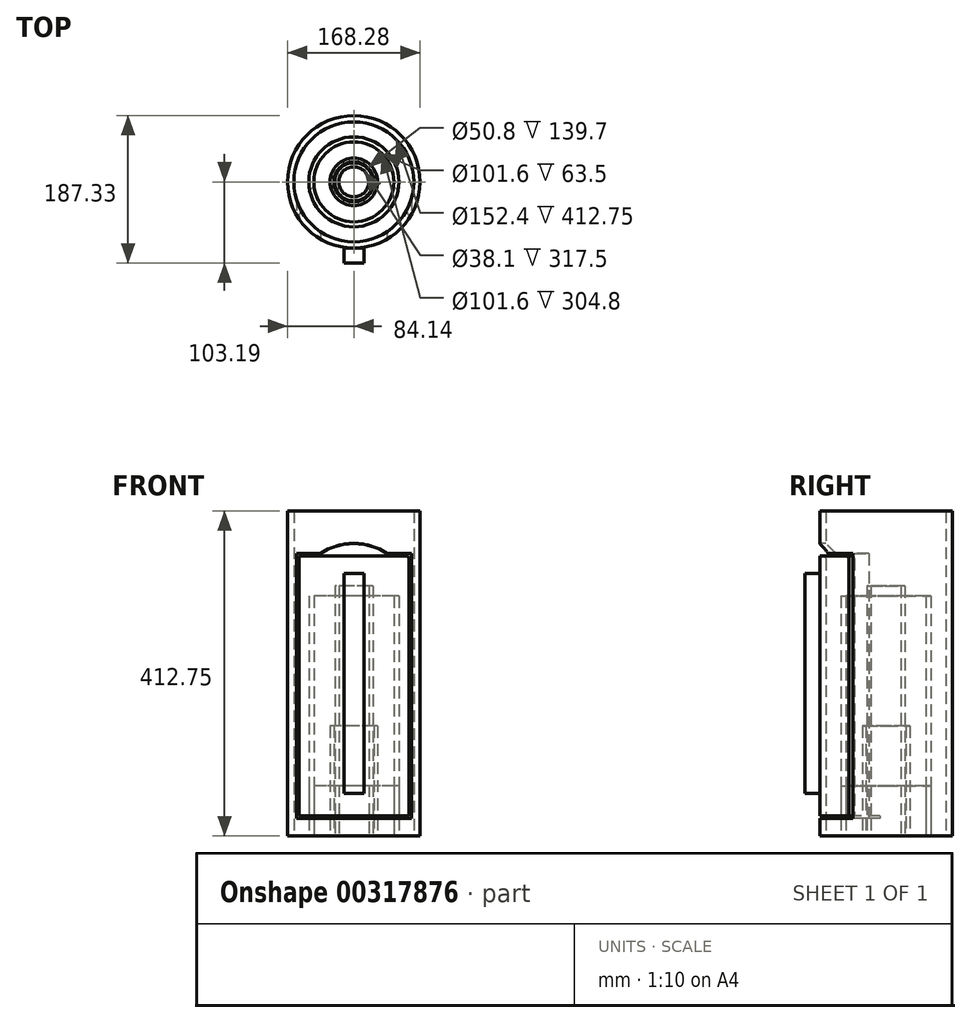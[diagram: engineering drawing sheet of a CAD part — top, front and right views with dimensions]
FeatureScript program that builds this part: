
annotation { "Feature Type Name" : "Feature", "Feature Type Description" : "" }
export const myFeature = defineFeature(function(context is Context, id is Id, definition is map)
    precondition{}
    {
        {
            var Q0;
            Q0=qCreatedBy(makeId("Top.planeOp"),FACE);
            var sketch = newSketch(context, id + "F0", { "sketchPlane" : qUnion([Q0])});
            skCircle(sketch, "E0", {"center": v(0, 0) * mm, "radius": 76.2 * mm});
            skCircle(sketch, "E1", {"center": v(0, 0) * mm, "radius": 84.14 * mm});
            skSolve(sketch);
        }
        {
            var Q0;
            Q0=makeQuery(id+"F0.imprint","IMPRINT",FACE,{"disambiguationData":[TD([[makeQuery(id+"F0.imprint","IMPRINT",EDGE,{"derivedFrom":sQuery(id+"F0.wireOp",EDGE,"E0")}),-1.0]])]});
            extrude(context, id + "F1", {"entities" : qUnion([Q0]), "depth" : 412.75 * mm});
        }
        {
            var Q0;
            Q0=qCreatedBy(makeId("Top.planeOp"),FACE);
            var sketch = newSketch(context, id + "F2", { "sketchPlane" : qUnion([Q0])});
            skCircle(sketch, "E2", {"center": v(0, 0) * mm, "radius": 50.8 * mm});
            skCircle(sketch, "E3", {"center": v(0, 0) * mm, "radius": 57.15 * mm});
            skSolve(sketch);
        }
        {
            var Q0;
            Q0=makeQuery(id+"F2.imprint","IMPRINT",FACE,{"disambiguationData":[TD([[makeQuery(id+"F2.imprint","IMPRINT",EDGE,{"derivedFrom":sQuery(id+"F2.wireOp",EDGE,"E2")}),-1.0]])]});
            extrude(context, id + "F3", {"entities" : qUnion([Q0]), "depth" : 63.5 * mm});
        }
        {
            var Q0;
            Q0=qCreatedBy(makeId("Top.planeOp"),FACE);
            var sketch = newSketch(context, id + "F4", { "sketchPlane" : qUnion([Q0])});
            skCircle(sketch, "E4", {"center": v(0, 0) * mm, "radius": 25.4 * mm});
            skCircle(sketch, "E5", {"center": v(0, 0) * mm, "radius": 30.16 * mm});
            skSolve(sketch);
        }
        {
            var Q0;
            Q0=makeQuery(id+"F4.imprint","IMPRINT",FACE,{"disambiguationData":[TD([[makeQuery(id+"F4.imprint","IMPRINT",EDGE,{"derivedFrom":sQuery(id+"F4.wireOp",EDGE,"E4")}),-1.0]])]});
            extrude(context, id + "F5", {"entities" : qUnion([Q0]), "depth" : 139.7 * mm});
        }
        {
            var Q0;
            Q0=qSketchRegion(id+"F2",true);
            extrude(context, id + "F6", {"entities" : qUnion([Q0]), "depth" : 304.8 * mm});
        }
        {
            var Q0;
            Q0=qCreatedBy(makeId("Top.planeOp"),FACE);
            var sketch = newSketch(context, id + "F7", { "sketchPlane" : qUnion([Q0])});
            skCircle(sketch, "E6", {"center": v(0, 0) * mm, "radius": 19.05 * mm});
            skCircle(sketch, "E7", {"center": v(0, 0) * mm, "radius": 24.13 * mm});
            skSolve(sketch);
        }
        {
            var Q0;
            Q0=makeQuery(id+"F7.imprint","IMPRINT",FACE,{"disambiguationData":[TD([[makeQuery(id+"F7.imprint","IMPRINT",EDGE,{"derivedFrom":sQuery(id+"F7.wireOp",EDGE,"E6")}),-1.0]])]});
            extrude(context, id + "F8", {"entities" : qUnion([Q0]), "depth" : 317.5 * mm});
        }
        {
            var Q0;
            Q0=qCreatedBy(makeId("Front.planeOp"),FACE);
            cPlane(context, id + "F9", {"entities" : qUnion([Q0]), "cplaneType" : CPlaneType.OFFSET, "offset" : 84.14 * mm, "width" : 152.4 * mm, "height" : 152.4 * mm});
        }
        {
            var Q0;
            Q0=qCreatedBy(id+"F9.planeOp",FACE);
            var sketch = newSketch(context, id + "F10", { "sketchPlane" : qUnion([Q0])});
            skLineSegment(sketch, "E8.bottom", {"start": v(-69.85, 25.4) * mm, "end": v(69.85, 25.4) * mm});
            skLineSegment(sketch, "E8.top", {"start": v(-69.85, 355.6) * mm, "end": v(69.85, 355.6) * mm});
            skLineSegment(sketch, "E8.left", {"start": v(-69.85, 25.4) * mm, "end": v(-69.85, 355.6) * mm});
            skLineSegment(sketch, "E8.right", {"start": v(69.85, 25.4) * mm, "end": v(69.85, 355.6) * mm});
            skLineSegment(sketch, "E9.0", {"start": v(-73.03, 22.23) * mm, "end": v(-73.03, 358.78) * mm});
            skLineSegment(sketch, "E9.1", {"start": v(-73.03, 22.23) * mm, "end": v(73.03, 22.23) * mm});
            skLineSegment(sketch, "E9.2", {"start": v(73.03, 22.23) * mm, "end": v(73.02, 358.78) * mm});
            skLineSegment(sketch, "E9.3", {"start": v(-73.03, 358.78) * mm, "end": v(73.02, 358.78) * mm});
            skSolve(sketch);
        }
        {
            var Q0;
            Q0=makeQuery(id+"F10.imprint","IMPRINT",FACE,{"disambiguationData":[TD([[makeQuery(id+"F10.imprint","IMPRINT",EDGE,{"derivedFrom":sQuery(id+"F10.wireOp",EDGE,"E8.bottom")}),-1.0]])]});
            extrude(context, id + "F11", {"entities" : qUnion([Q0]), "operationType" : NewBodyOperationType.REMOVE, "oppositeDirection" : true, "depth" : 76.2 * mm});
        }
        {
            var Q0;
            Q0=qCreatedBy(id+"F9.planeOp",FACE);
            var sketch = newSketch(context, id + "F12", { "sketchPlane" : qUnion([Q0])});
            skLineSegment(sketch, "E10.0", {"start": v(69.85, 25.4) * mm, "end": v(-69.85, 25.4) * mm});
            skPoint(sketch, "E11", {"position": v(0, 25.4) * mm});
            skSolve(sketch);
        }
        {
            var Q0;
            Q0=makeQuery(id+"F11.boolean.opBoolean","INTERSECT",EDGE,{"derivedFrom":[makeQuery(id+"F1.opExtrude","SWEPT_FACE",FACE,{"disambiguationData":[OSD([sQuery(id+"F0.wireOp",EDGE,"E0")])]}),makeQuery(id+"F11.opExtrude","SWEPT_FACE",FACE,{"disambiguationData":[OSD([sQuery(id+"F10.wireOp",EDGE,"E8.right")])]})]});
            var Q1;
            Q1=makeQuery(id+"F11.boolean.opBoolean","INTERSECT",EDGE,{"derivedFrom":[makeQuery(id+"F1.opExtrude","SWEPT_FACE",FACE,{"disambiguationData":[OSD([sQuery(id+"F0.wireOp",EDGE,"E0")])]}),makeQuery(id+"F11.opExtrude","SWEPT_FACE",FACE,{"disambiguationData":[OSD([sQuery(id+"F10.wireOp",EDGE,"E8.left")])]})]});
            fillet(context, id + "F13", {"entities" : qUnion([Q0, Q1]), "radius" : 3.17 * mm, "tangentPropagation" : true, "allowEdgeOverflow" : false});
        }
        {
            var Q0;
            Q0=makeQuery(id+"F13.opFillet","BLEND_EDGE",EDGE,{"blendedFrom":[makeQuery(id+"F11.boolean.opBoolean","INTERSECT",EDGE,{"derivedFrom":[makeQuery(id+"F1.opExtrude","SWEPT_FACE",FACE,{"disambiguationData":[OSD([sQuery(id+"F0.wireOp",EDGE,"E0")])]}),makeQuery(id+"F11.opExtrude","SWEPT_FACE",FACE,{"disambiguationData":[OSD([sQuery(id+"F10.wireOp",EDGE,"E8.right")])]})]}),makeQuery(id+"F11.boolean.opBoolean","COPY",FACE,{"derivedFrom":makeQuery(id+"F11.opExtrude","SWEPT_FACE",FACE,{"disambiguationData":[OSD([sQuery(id+"F10.wireOp",EDGE,"E8.top")])]})})],"blendedInto":[makeQuery(id+"F11.boolean.opBoolean","COPY",FACE,{"derivedFrom":makeQuery(id+"F11.opExtrude","SWEPT_FACE",FACE,{"disambiguationData":[OSD([sQuery(id+"F10.wireOp",EDGE,"E8.top")])]})})]});
            var Q1;
            Q1=makeQuery(id+"F13.opFillet","BLEND_EDGE",EDGE,{"blendedFrom":[makeQuery(id+"F11.boolean.opBoolean","INTERSECT",EDGE,{"derivedFrom":[makeQuery(id+"F1.opExtrude","SWEPT_FACE",FACE,{"disambiguationData":[OSD([sQuery(id+"F0.wireOp",EDGE,"E0")])]}),makeQuery(id+"F11.opExtrude","SWEPT_FACE",FACE,{"disambiguationData":[OSD([sQuery(id+"F10.wireOp",EDGE,"E8.left")])]})]}),makeQuery(id+"F11.boolean.opBoolean","COPY",FACE,{"derivedFrom":makeQuery(id+"F11.opExtrude","SWEPT_FACE",FACE,{"disambiguationData":[OSD([sQuery(id+"F10.wireOp",EDGE,"E8.top")])]})})],"blendedInto":[makeQuery(id+"F11.boolean.opBoolean","COPY",FACE,{"derivedFrom":makeQuery(id+"F11.opExtrude","SWEPT_FACE",FACE,{"disambiguationData":[OSD([sQuery(id+"F10.wireOp",EDGE,"E8.top")])]})})]});
            fillet(context, id + "F14", {"entities" : qUnion([Q0, Q1]), "radius" : 3.17 * mm, "tangentPropagation" : true, "allowEdgeOverflow" : false});
        }
        {
            var Q0;
            Q0=qCreatedBy(id+"F9.planeOp",FACE);
            var sketch = newSketch(context, id + "F15", { "sketchPlane" : qUnion([Q0])});
            skLineSegment(sketch, "E12.0", {"start": v(73.02, 358.78) * mm, "end": v(-73.03, 358.78) * mm});
            skCircle(sketch, "E13", {"center": v(0, 295.28) * mm, "radius": 76.2 * mm});
            skPoint(sketch, "E13.centerSnap0", {"position": v(0, 358.78) * mm});
            skPoint(sketch, "E14", {"position": v(0, 371.48) * mm});
            skSolve(sketch);
        }
        {
            var Q0;
            {var subQ0=sQuery(id+"F15.wireOp",EDGE,"E13");var subQ1=sQuery(id+"F15.wireOp",EDGE,"E12.0");var subQ2=makeQuery(id+"F15.imprint","INTERSECT",VERTEX,{"disambiguationData":[OD(0.0)],"derivedFrom":[subQ1,subQ0]});Q0=makeQuery(id+"F15.imprint","IMPRINT",FACE,{"disambiguationData":[TD([[makeQuery(id+"F15.imprint","IMPRINT",EDGE,{"disambiguationData":[TD([[subQ2,1.0]])],"derivedFrom":subQ1}),-1.0]])]});}
            extrude(context, id + "F16", {"entities" : qUnion([Q0]), "operationType" : NewBodyOperationType.REMOVE, "oppositeDirection" : true, "depth" : 25.4 * mm});
        }
        {
            var Q0;
            Q0=qCreatedBy(id+"F9.planeOp",FACE);
            var sketch = newSketch(context, id + "F17", { "sketchPlane" : qUnion([Q0])});
            skLineSegment(sketch, "E15.bottom", {"start": v(-12.7, 333.38) * mm, "end": v(12.7, 333.38) * mm});
            skLineSegment(sketch, "E15.top", {"start": v(-12.7, 53.98) * mm, "end": v(12.7, 53.98) * mm});
            skLineSegment(sketch, "E15.left", {"start": v(-12.7, 333.38) * mm, "end": v(-12.7, 53.97) * mm});
            skLineSegment(sketch, "E15.right", {"start": v(12.7, 333.38) * mm, "end": v(12.7, 53.97) * mm});
            skSolve(sketch);
        }
        {
            var Q0;
            Q0=makeQuery(id+"F17.imprint","IMPRINT",FACE,{"disambiguationData":[TD([[makeQuery(id+"F17.imprint","IMPRINT",EDGE,{"derivedFrom":sQuery(id+"F17.wireOp",EDGE,"E15.bottom")}),-1.0]])]});
            extrude(context, id + "F18", {"entities" : qUnion([Q0]), "depth" : 19.05 * mm});
        }
        {
            var Q0;
            Q0=qCreatedBy(id+"F9.planeOp",FACE);
            var sketch = newSketch(context, id + "F19", { "sketchPlane" : qUnion([Q0])});
            skLineSegment(sketch, "E16.0.0", {"start": v(-12.7, 333.38) * mm, "end": v(-12.7, 53.97) * mm, "construction": true});
            skLineSegment(sketch, "E16.0.1", {"start": v(-12.7, 53.98) * mm, "end": v(12.7, 53.98) * mm, "construction": true});
            skLineSegment(sketch, "E16.0.2", {"start": v(12.7, 53.97) * mm, "end": v(12.7, 333.38) * mm, "construction": true});
            skLineSegment(sketch, "E16.0.3", {"start": v(12.7, 333.38) * mm, "end": v(-12.7, 333.38) * mm, "construction": true});
            skLineSegment(sketch, "E17", {"start": v(12.7, 193.68) * mm, "end": v(-12.7, 193.68) * mm, "construction": true});
            skPoint(sketch, "E18", {"position": v(0, 193.68) * mm});
            skSolve(sketch);
        }
    });
